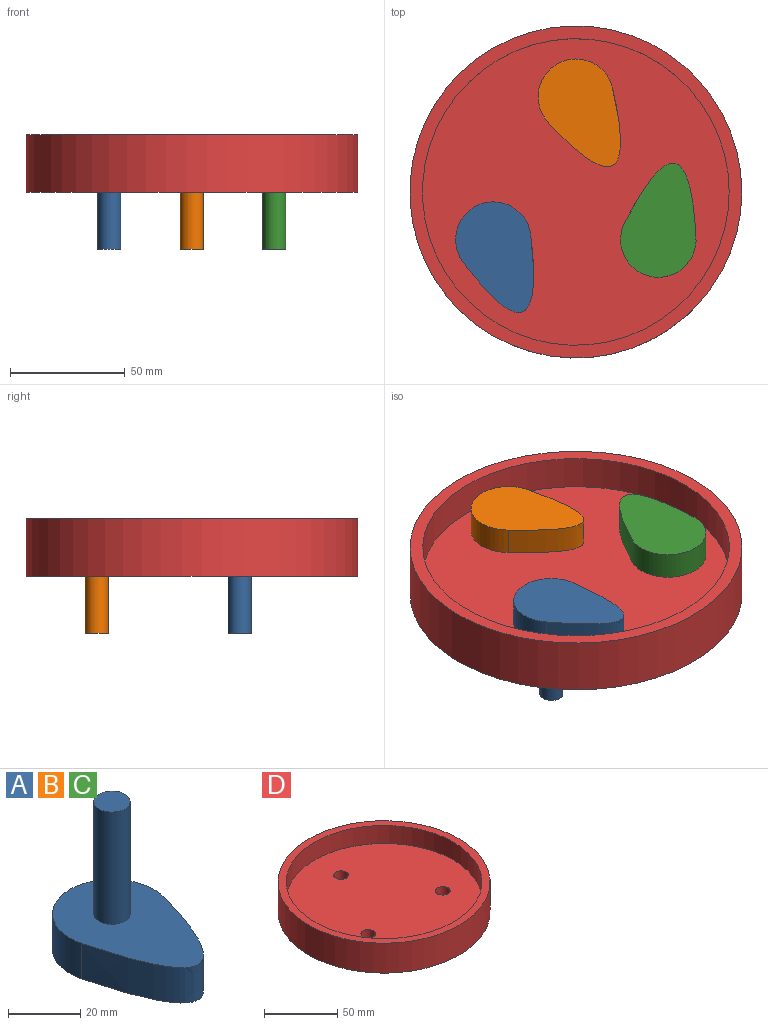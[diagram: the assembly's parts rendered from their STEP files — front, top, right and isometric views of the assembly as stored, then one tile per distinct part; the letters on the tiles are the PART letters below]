
ASSEMBLY  parts=4 mates=3
PART A: 6 faces, bbox 32.9x61.5x50 mm
  f0: cylinder r=16.46mm len=32.93mm, axis (0,0,-1), area 728mm2, adj f1,f2,f3
  f1: extruded ~31.71x29.88mm, area 837.6mm2, adj f0,f2,f3
  f2: plane 61.5x32.93mm, normal (0,0,1), area 1113.9mm2, adj f0,f1,f4
  f3: plane 61.5x32.93mm, normal (0,0,-1), area 1194.1mm2, adj f0,f1
  f4: cylinder r=5.05mm len=38mm, axis (0,0,-1), area 1205.7mm2, adj f2,f5
  f5: plane 10.1x10.1mm, normal (0,0,1), area 80.1mm2, adj f4
PART B: same geometry as A
PART C: same geometry as A
PART D: 8 faces, bbox 144.9x144.9x25 mm
  f0: cylinder r=5mm len=10mm, axis (0,0,-1), area 314.2mm2, adj f3,f4
  f1: cylinder r=5mm len=10mm, axis (0,0,-1), area 314.2mm2, adj f3,f4
  f2: cylinder r=5mm len=10mm, axis (0,0,-1), area 314.2mm2, adj f3,f4
  f3: plane 133.84x133.84mm, normal (0,0,1), area 13833.8mm2, adj f0,f1,f2,f5
  f4: plane 144.92x144.92mm, normal (0,0,-1), area 16260mm2, adj f0,f1,f2,f6
  f5: cylinder r=66.92mm len=133.84mm, axis (0,0,-1), area 6307.2mm2, adj f3,f7
  f6: cylinder r=72.46mm len=144.92mm, axis (0,0,-1), area 11382.3mm2, adj f4,f7
  f7: plane 144.92x144.92mm, normal (0,0,1), area 2426.1mm2, adj f5,f6
PLACE A rot(axis=(0.18,-0.98,0),180deg) t=(-74.36,-117.27,96.34)mm
PLACE B rot(axis=(0.24,-0.97,0),180deg) t=(-28.31,-67.43,96.34)mm
PLACE C rot(axis=(0.99,-0.11,0),180deg) t=(271.31,-25.13,96.34)mm
PLACE D t=(84.35,-8.46,71.34)mm fixed
MATE revolute D.f2 <-> C.f0  axis (0,0,1) through (120.36,-29.25,81.34)mm
MATE revolute D.f1 <-> A.f0  axis (0,0,1) through (48.34,-29.25,81.34)mm
MATE revolute D.f0 <-> B.f0  axis (0,0,1) through (84.35,33.12,81.34)mm
